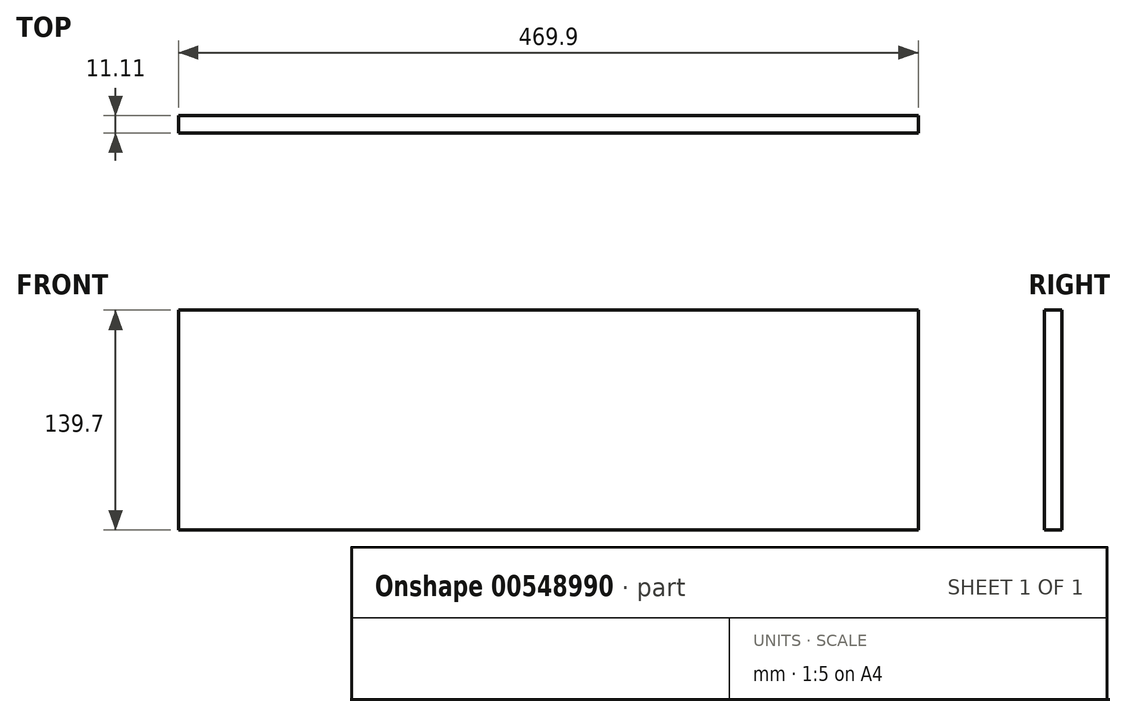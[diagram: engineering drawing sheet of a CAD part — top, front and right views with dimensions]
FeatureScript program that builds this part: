
annotation { "Feature Type Name" : "Feature", "Feature Type Description" : "" }
export const myFeature = defineFeature(function(context is Context, id is Id, definition is map)
    precondition{}
    {
        {
            var Q0;
            Q0=qCreatedBy(makeId("Front.planeOp"),FACE);
            var sketch = newSketch(context, id + "F0", { "sketchPlane" : qUnion([Q0])});
            skLineSegment(sketch, "E0.bottom", {"start": v(234.95, -69.85) * mm, "end": v(-234.95, -69.85) * mm});
            skLineSegment(sketch, "E0.top", {"start": v(234.95, 69.85) * mm, "end": v(-234.95, 69.85) * mm});
            skLineSegment(sketch, "E0.left", {"start": v(234.95, -69.85) * mm, "end": v(234.95, 69.85) * mm});
            skLineSegment(sketch, "E0.right", {"start": v(-234.95, -69.85) * mm, "end": v(-234.95, 69.85) * mm});
            skPoint(sketch, "E0.middle", {"position": v(0, 0) * mm});
            skSolve(sketch);
        }
        {
            var Q0;
            Q0 = qSketchRegion(id + "F0", true);
            extrude(context, id + "F1", {"entities" : qUnion([Q0]), "depth" : 11.1 * mm, "offsetDistance" : 25.4 * mm});
        }
    });
